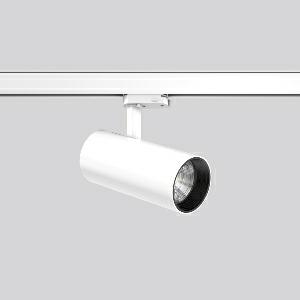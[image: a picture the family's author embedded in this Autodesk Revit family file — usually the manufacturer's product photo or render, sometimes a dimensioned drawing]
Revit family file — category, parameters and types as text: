
# Revit family: deecos_s_mini_742209_002_2_965f
name_source: partatom
category: Lighting Fixtures
units: mm (PartAtom-declared; Revit-internal decimal feet)

## family parameters
Cut with Voids When Loaded = No
Host = Face
Light Source = No
Part Type = Normal
Room Calculation Point = No
Round Connector Dimension = Use Diameter
Shared = No

## types (1)
- DEECOS S mini (1 x LED Modul 927, 3050 lm, 2700)
    Apparent Load = 29 VA
    Approval mark = CE
    CIE Flux Codes = 80 99 100 100 100
    Color Rendering = 92
    Color Temperature = 2700
    Default Elevation = 1800 mm
    Description = Series: DEECOS S mini
LED surface-mounted projector in modern design with no visible cooling ribs. Housing: die-cast aluminium, powder-coated. Rotation range: 356°. Swivel range: 90°. Black plastic ring and recessed LED to prevent glare from the side. Optical assembly with lens made of plastic (polycarbonate) for the best homogeneous light distribution - can be changed without tools. Best colour rendering index Ra>90. With multi adaptor for 3-circuit tracks 230 V. Suitable for Track on ceiling, Wall track. High quality converter without flickering and stroboscopic effect. The following accessories can be mounted without use of tools: interchangeable lenses, decorative glasses, honeycomb louvre, clear and frosted diffusers, white interchangeable plastic ring. 
Colour: traffic white, matt (RAL 9016)
Diameter: 87 mm
Height: 214 mm
Lamp: LED
Socket: without socket
Colour temperature: 2700K
Colour rendering index (CRI): 92
System power: 29 W
Rated luminous flux: 3050 lm
Luminous efficiency: 105 lm/W
Control gear: Regulated power supply
Protection class: I
Type of protection: IP 20
    Height = 214 mm
    Lamp = 1 x LED Modul 927
    Lamp Light Flux = 3050 lm
    Lamp count = 1
    Length = 87 mm
    Lifetime = 50000 h
    Luminous efficacy = 105 lm/W
    Manufacturer = RZB
    ModVariant = No
    Model = 742209.002.2
    Mounting Place = Ceiling
    Mounting Type = Rail mounted
    Number of Poles = 1
    OnlyDefault = Yes
    Power Factor = 1
    Product Name = DEECOS S mini
    Product group = Track mounted projectors
    ProductGroupID = 301
    Protection Class = Protection class I
    Protection Degree = IP 20
    RLX_Detail_Level = 1
    RLX_Emergency_Light_Flux = 0 lm
    RLX_Emergency_Type = 0
    RLX_Emergency_Type_DB = No
    RlxData = <blob elided: 35725 chars, md5=6051bf29>
    Socket = socket
    Standby Power = 0 W
    System Light Flux = 3050 lm
    System Power = 29 W
    Type Comments = Product without accessories
    Type Image = 741930.002.jpg
    URL = http://relux.com
    VarID = ---
    Voltage = 230 V
    Voltage Range = 220-240 V
    Weight = 0.00 kg
    Width = 0 mm  [stored 0 ft]

note: [stored X ft] marks values corroborated as IEEE doubles in the binary element streams (Revit-internal decimal feet)

## geometry (parser evidence)
native form markers: Blend x4, Sweep x12
no freeform markers — native parametric forms only
